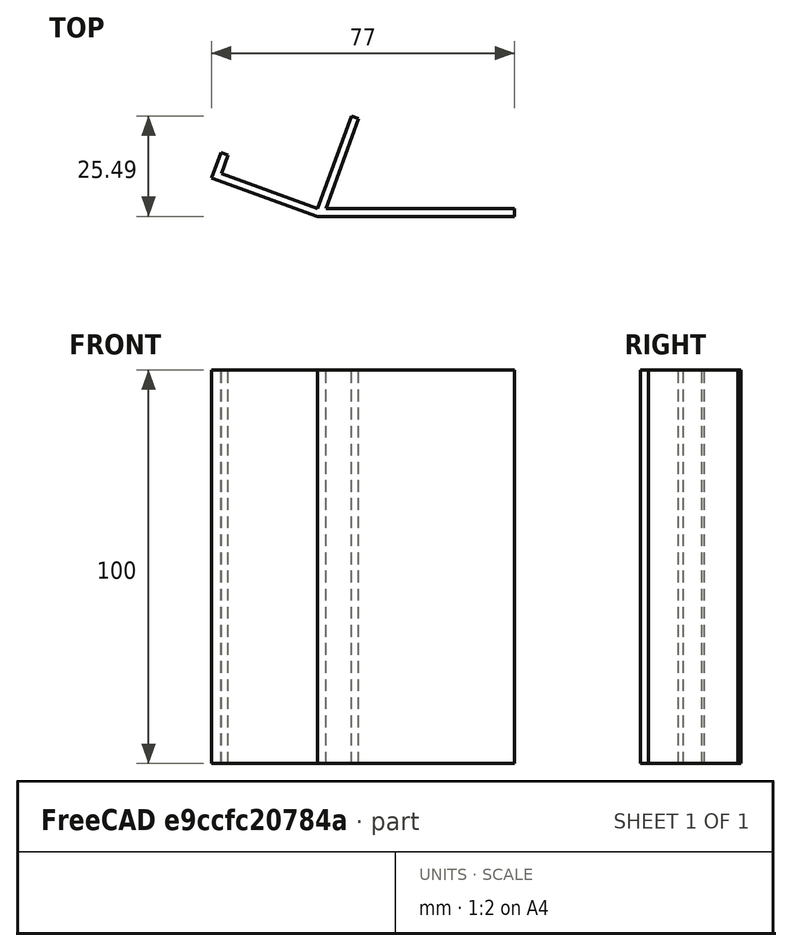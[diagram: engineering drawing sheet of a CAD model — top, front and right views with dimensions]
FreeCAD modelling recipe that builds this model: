
FCSTD DOCUMENT  (FreeCAD 0.21R33771 (Git))
Label: Frame75Stand
License: All rights reserved
LicenseURL: https://en.wikipedia.org/wiki/All_rights_reserved
objects: Sketcher::SketchObject×1, PartDesign::Pad×1, PartDesign::Body×1
note: 4 computed .brp shape members not serialized (recipe doc carries the construction recipe); baked Part::Feature solids carry a one-line shape summary decoded from their .brp

FEATURE [Sketcher::SketchObject] Sketch  label="StandS"
  FullyConstrained = true
  MapMode = 5
  Support = -> [XY_Plane]
  sketch-geometry (11):
    g0: LineSegment StartX=0 StartY=0 StartZ=0 EndX=50 EndY=0 EndZ=0
    g1: LineSegment StartX=50 StartY=0 StartZ=0 EndX=50 EndY=2 EndZ=0
    g2: LineSegment StartX=50 StartY=2 StartZ=0 EndX=2.12837 EndY=2 EndZ=0
    g3: LineSegment StartX=2.12837 StartY=2 StartZ=0 EndX=10.4299 EndY=24.8083 EndZ=0
    g4: LineSegment StartX=10.4299 StartY=24.8083 StartZ=0 EndX=8.55052 EndY=25.4923 EndZ=0
    g5: LineSegment StartX=8.55052 StartY=25.4923 StartZ=0 EndX=1.8631e-05 EndY=2 EndZ=0
    g6: LineSegment StartX=1.8631e-05 StartY=2 StartZ=0 EndX=-24.432 EndY=10.8925 EndZ=0
    g7: LineSegment StartX=-26.9954 StartY=9.69718 StartZ=0 EndX=0 EndY=0 EndZ=0
    g8: LineSegment StartX=-26.9954 StartY=9.69718 StartZ=0 EndX=-24.6013 EndY=16.275 EndZ=0
    g9: LineSegment StartX=-24.6013 StartY=16.275 StartZ=0 EndX=-22.7219 EndY=15.591 EndZ=0
    g10: LineSegment StartX=-22.7219 StartY=15.591 StartZ=0 EndX=-24.432 EndY=10.8925 EndZ=0
  constraints (32):
    c: Horizontal(g0)
    c: Coincident(g0,g1)
    c: Vertical(g1)
    c: Coincident(g1,g2)
    c: Horizontal(g2)
    c: Coincident(g2,g3)
    c: Coincident(g3,g4)
    c: Coincident(g4,g5)
    c: Coincident(g5,g6)
    c: Coincident(g0,g7)
    c: Coincident(g0,g-1)
    c: Distance(g4) = 2
    c: Distance(g1) = 2
    c: Distance(g0) = 50
    c: Coincident(g8,g9)
    c: Coincident(g9,g10)
    c: Coincident(g6,g10)
    c: Coincident(g7,g8)
    c: Distance(g9) = 2
    c: Distance(g10) = 5
    c: Distance(g5) = 25
    c: Angle(g5,g6) = 1.5708
    c: DistanceY(g2,g5) = 0
    c: Angle(g6,g10) = 1.5708
    c: Distance(g8) = 7
    c: Angle(g9,g10) = 1.5708
    c: Angle(g8,g9) = 1.5708
    c: Angle(g5,g4) = 1.5708
    c: Angle(g4,g3) = 1.5708
    c: Distance(g6) = 26
    c: Distance(g0,g5) = 2
    c: Angle(g2,g3) = 1.22173
FEATURE [PartDesign::Pad] Pad  label="Stand"
  Direction = (0,0,1)
  Length = 100
  Length2 = 10
  Profile = -> Sketch
  ReferenceAxis = -> Sketch [N_Axis]
  Type = 0
FEATURE [PartDesign::Body] Body
  Group = -> [Sketch,Pad]
  Origin = -> Origin
  Tip = -> Pad
